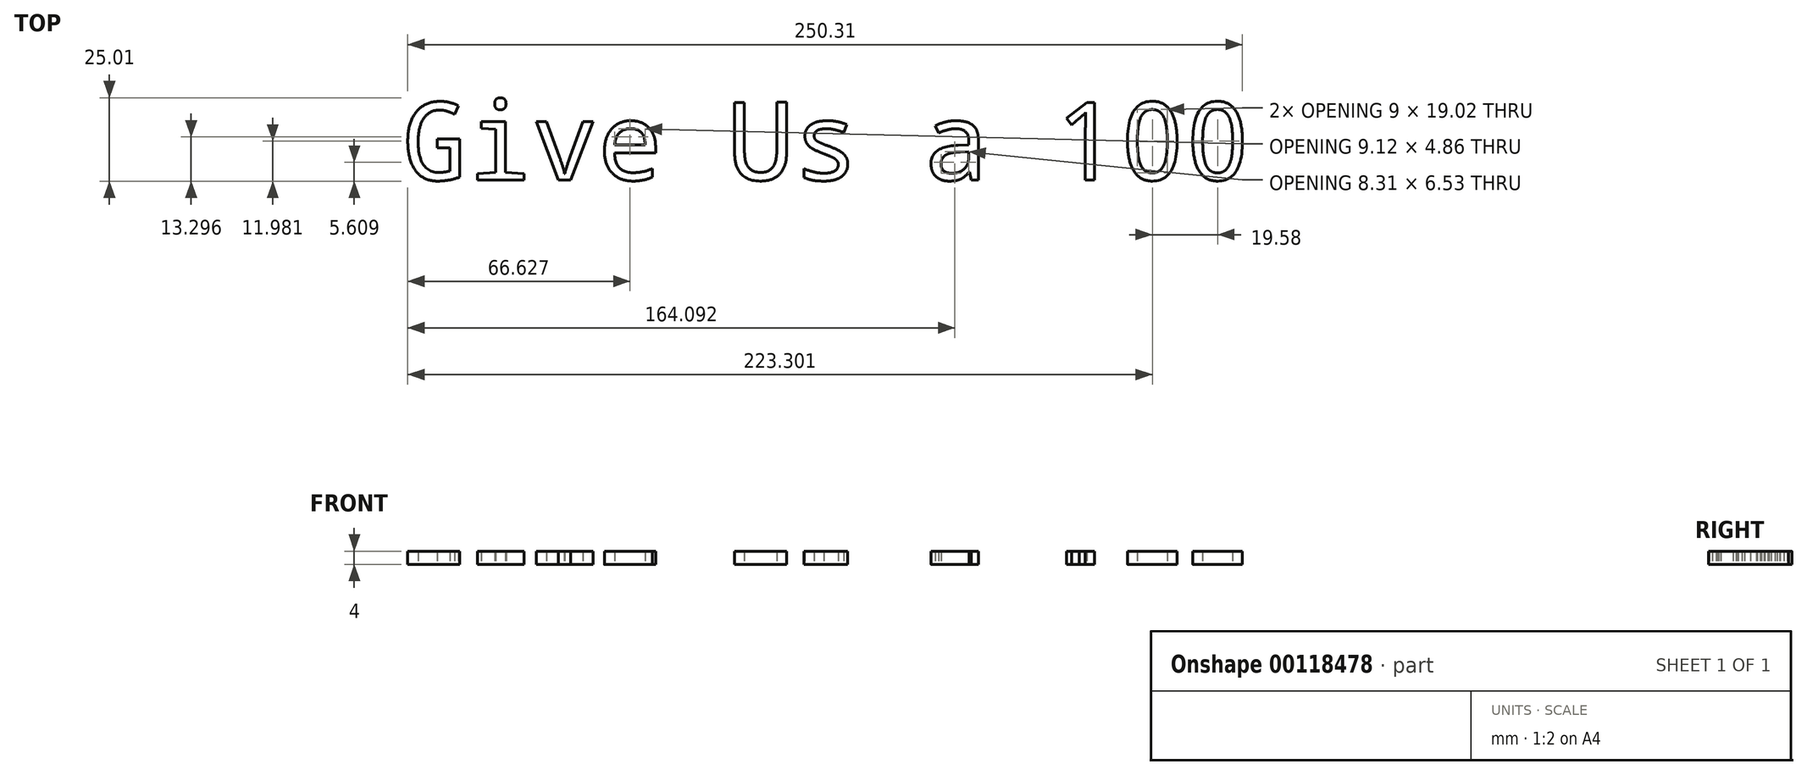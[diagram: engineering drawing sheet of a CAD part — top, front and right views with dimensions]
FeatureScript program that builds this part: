
annotation { "Feature Type Name" : "Feature", "Feature Type Description" : "" }
export const myFeature = defineFeature(function(context is Context, id is Id, definition is map)
    precondition{}
    {
        {
            var Q0;
            Q0=qCreatedBy(makeId("Top.planeOp"),FACE);
            var sketch = newSketch(context, id + "F0", { "sketchPlane" : qUnion([Q0])});
            skText(sketch, "E0", { "text": "Give Us a 100", "fontName": "DroidSansMono.ttf"});
            const initialGuessF0  = {"E0": [-0.0684, 0.03092, 1, 0, 0.02349]};
            skSetInitialGuess(sketch, initialGuessF0);
            skSolve(sketch);
        }
        {
            var Q0;
            Q0 = qSketchRegion(id + "F0", true);
            extrude(context, id + "F1", {"entities" : qUnion([Q0]), "depth" : 4 * mm});
        }
    });
